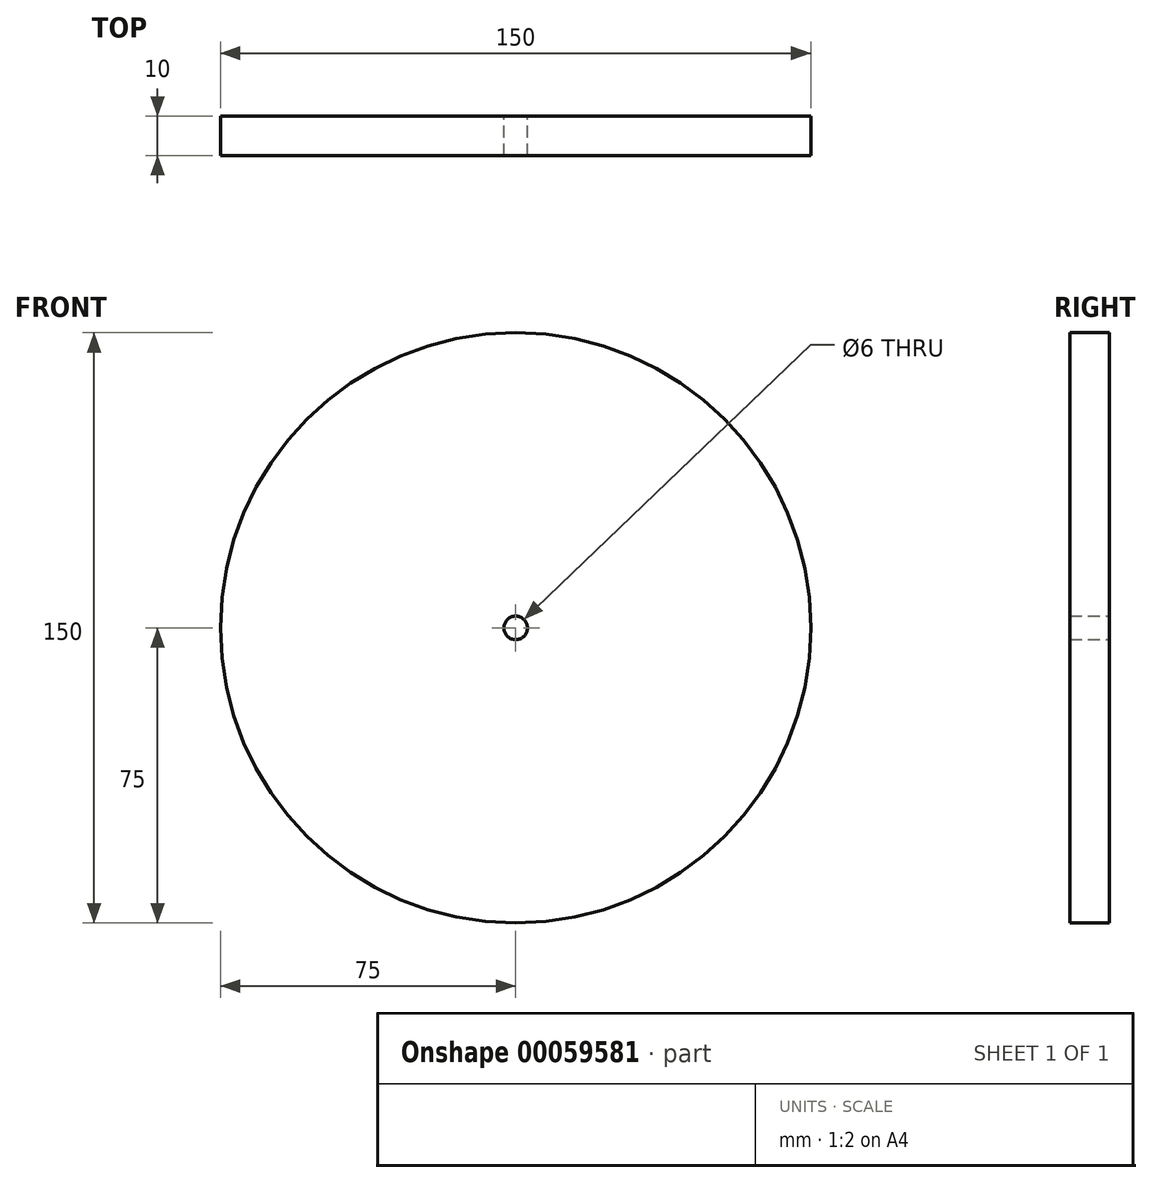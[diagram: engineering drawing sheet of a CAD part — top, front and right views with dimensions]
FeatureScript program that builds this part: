
annotation { "Feature Type Name" : "Feature", "Feature Type Description" : "" }
export const myFeature = defineFeature(function(context is Context, id is Id, definition is map)
    precondition{}
    {
        {
            var Q0;
            Q0=qCreatedBy(makeId("Front.planeOp"),FACE);
            var sketch = newSketch(context, id + "F0", { "sketchPlane" : qUnion([Q0])});
            skCircle(sketch, "E0", {"center": v(0, 0) * mm, "radius": 75 * mm});
            skCircle(sketch, "E1", {"center": v(0, 0) * mm, "radius": 3 * mm});
            skSolve(sketch);
        }
        {
            var Q0;
            Q0=makeQuery(id+"F0.imprint","IMPRINT",FACE,{"disambiguationData":[TD([[makeQuery(id+"F0.imprint","IMPRINT",EDGE,{"derivedFrom":sQuery(id+"F0.wireOp",EDGE,"E0")}),1.0]])]});
            extrude(context, id + "F1", {"entities" : qUnion([Q0]), "depth" : 10 * mm});
        }
    });
